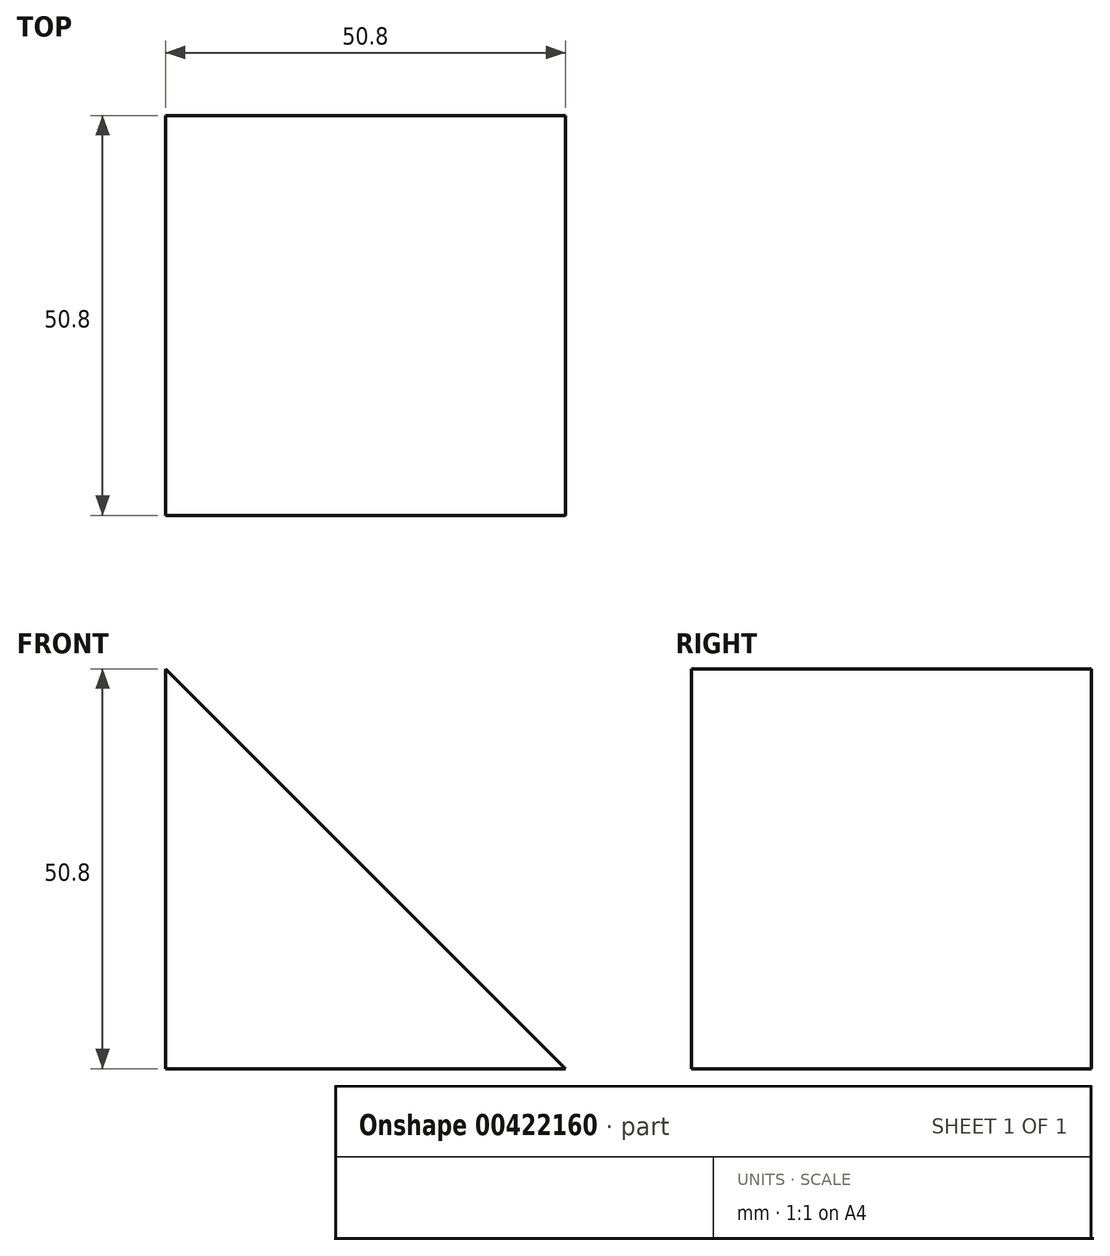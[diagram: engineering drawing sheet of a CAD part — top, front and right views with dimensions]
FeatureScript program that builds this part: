
annotation { "Feature Type Name" : "Feature", "Feature Type Description" : "" }
export const myFeature = defineFeature(function(context is Context, id is Id, definition is map)
    precondition{}
    {
        {
            var Q0;
            Q0=qCreatedBy(makeId("Front.planeOp"),FACE);
            var sketch = newSketch(context, id + "F0", { "sketchPlane" : qUnion([Q0])});
            skLineSegment(sketch, "E0", {"start": v(-42.82, 47.15) * mm, "end": v(-42.82, -3.65) * mm});
            skLineSegment(sketch, "E1", {"start": v(-42.82, -3.65) * mm, "end": v(7.98, -3.65) * mm});
            skLineSegment(sketch, "E2", {"start": v(-42.82, 47.15) * mm, "end": v(7.98, -3.65) * mm});
            skSolve(sketch);
        }
        {
            var Q0;
            Q0 = qSketchRegion(id + "F0", true);
            extrude(context, id + "F1", {"entities" : qUnion([Q0]), "depth" : 50.8 * mm});
        }
    });
